# Revit family: Mini MP 240 Comb (a)
name_source: partatom
category: Equipement spécialisé
revit_build: Autodesk Revit LT 2015 (Build: 20140606_1530(x64)
units: mm (PartAtom-declared; Revit-internal decimal feet)

## types (5) — shared parameters
Apparent Power = 0 VA
Depth Electrique connexion cloche = 39 mm  [stored 0.127953 ft]
Depth Electrique connexion fouet = 44 mm
Depth cloche = 78 mm  [stored 0.255906 ft]
Depth fouet = 87 mm
Description = MIXERS PLONGEANTS GAMME MINI
Fabricant = ROBOT COUPE
Height Electrique connexion cloche = 520 mm
Height Electrique connexion fouet = 540 mm
Height cloche = 530 mm
Height fouet = 550 mm
Phase = 1
Speeds (Rpm) = 2000 to 12500 (mixer)  -  350 to 1560 (whisk)
URL = www.robot-coupe.com
Width cloche = 115 mm
Width fouet = 115 mm
water = Connector
zero-valued in all types: Cold water supply, Cold water supply height, Used water, Waste water height

## per-type parameters (varying)
| type | Amps | Cycle | Modèle | Volts | Watts | Weight |
| Mini MP 240 Combi   230/50/1 | 2.1 A | 50 Hz | Mini MP 240 Combi | 230 V | 270 W | 2.8 kg |
| Mini MP 240 Combi   240/50/1 | 2.1 A | 50 Hz | Mini MP 240 Combi | 240 V | 270 W | 2.8 kg |
| Mini MP 240 Combi   120/60/1 | 2.6 A | 60 Hz | Mini MP 240 Combi | 120 V | 270 W | 2.8 kg |
| Mini MP 240 Combi   220/60/1 | 1.4 A | 60 Hz | Mini MP 240 Combi | 220 V | 270 W | 2.8 kg |
| Mini MP 240 Combi USA   120/60/1 | 2.1 A | 60 Hz | MMP 240 Combi | 120 V | 290 W | 7 lbs |

note: [stored X ft] marks values corroborated as IEEE doubles in the binary element streams (Revit-internal decimal feet)

## geometry (parser evidence)
native form markers: Blend x104, Sweep x4
no freeform markers — native parametric forms only
